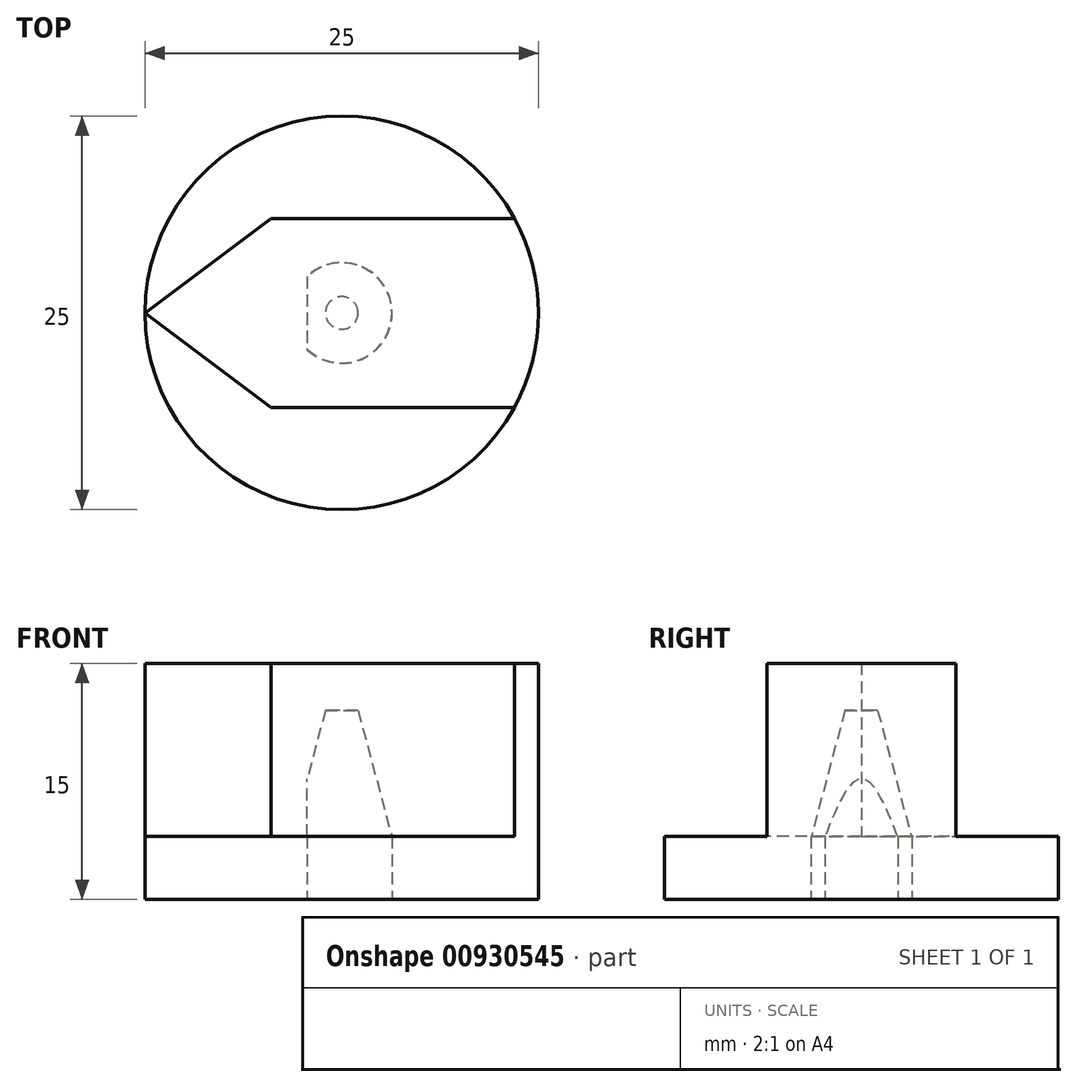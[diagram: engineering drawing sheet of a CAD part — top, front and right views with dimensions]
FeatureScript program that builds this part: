
annotation { "Feature Type Name" : "Feature", "Feature Type Description" : "" }
export const myFeature = defineFeature(function(context is Context, id is Id, definition is map)
    precondition{}
    {
        {
            var Q0;
            Q0=qCreatedBy(makeId("Top.planeOp"),FACE);
            var sketch = newSketch(context, id + "F0", { "sketchPlane" : qUnion([Q0])});
            skCircle(sketch, "E0", {"center": v(0, 0) * mm, "radius": 3.2 * mm, "construction": true});
            skLineSegment(sketch, "E1", {"start": v(-2.2, 2.32) * mm, "end": v(-2.2, -2.32) * mm});
            skLineSegment(sketch, "E2", {"start": v(3.2, 0) * mm, "end": v(-2.2, 0) * mm, "construction": true});
            skArc(sketch, "E3", {"start": v(-2.2, -2.32) * mm, "mid": v(3.2, 0) * mm, "end": v(-2.2, 2.32) * mm});
            skCircle(sketch, "E4", {"center": v(0, 0) * mm, "radius": 12.5 * mm});
            skSolve(sketch);
        }
        {
            var Q0;
            Q0=qSketchRegion(id+"F0",true);
            extrude(context, id + "F1", {"entities" : qUnion([Q0]), "depth" : 4 * mm, "offsetDistance" : 25 * mm});
        }
        {
            var Q0;
            Q0=makeQuery(id+"F1.opExtrude","CAP_FACE",FACE,{"disambiguationData":[OSD([sQuery(id+"F0.wireOp",EDGE,"E1"),sQuery(id+"F0.wireOp",EDGE,"E3"),sQuery(id+"F0.wireOp",EDGE,"E4")])],"isStart":false});
            var sketch = newSketch(context, id + "F2", { "sketchPlane" : qUnion([Q0])});
            skLineSegment(sketch, "E5", {"start": v(-12.5, 0) * mm, "end": v(-4.5, 6) * mm});
            skLineSegment(sketch, "E6", {"start": v(-4.5, 6) * mm, "end": v(10.97, 6) * mm});
            skArc(sketch, "E7", {"start": v(12.5, 0) * mm, "mid": v(12.11, 3.1) * mm, "end": v(10.97, 6) * mm});
            skLineSegment(sketch, "E8", {"start": v(-12.5, 0) * mm, "end": v(12.5, 0) * mm, "construction": true});
            skLineSegment(sketch, "E9.MirrorCS", {"start": v(-12.5, 0) * mm, "end": v(-4.5, -6) * mm});
            skLineSegment(sketch, "E10.MirrorCS", {"start": v(-4.5, -6) * mm, "end": v(10.97, -6) * mm});
            skArc(sketch, "E11.MirrorCS", {"start": v(12.5, 0) * mm, "mid": v(12.11, -3.1) * mm, "end": v(10.97, -6) * mm});
            skCircle(sketch, "E12", {"center": v(0, 0) * mm, "radius": 0.5 * mm});
            skSolve(sketch);
        }
        {
            var Q0;
            Q0=qSketchRegion(id+"F2",true);
            extrude(context, id + "F3", {"entities" : qUnion([Q0]), "operationType" : NewBodyOperationType.ADD, "depth" : 8 * mm, "offsetDistance" : 25 * mm});
        }
        {
            var Q0;
            Q0=makeQuery(id+"F3.opExtrude","CAP_EDGE",EDGE,{"disambiguationData":[OSD([sQuery(id+"F2.wireOp",EDGE,"E12")])],"isStart":true});
            chamfer(context, id + "F4", {"entities" : qUnion([Q0]), "chamferType" : ChamferType.OFFSET_ANGLE, "width" : 10 * mm, "oppositeDirection" : true, "angle" : 15 * degree, "tangentPropagation" : true});
        }
        {
            var Q0;
            Q0=makeQuery(id+"F3.opExtrude","CAP_FACE",FACE,{"disambiguationData":[OSD([sQuery(id+"F2.wireOp",EDGE,"E5"),sQuery(id+"F2.wireOp",EDGE,"E6"),sQuery(id+"F2.wireOp",EDGE,"E7"),sQuery(id+"F2.wireOp",EDGE,"E9.MirrorCS"),sQuery(id+"F2.wireOp",EDGE,"E10.MirrorCS"),sQuery(id+"F2.wireOp",EDGE,"E11.MirrorCS"),sQuery(id+"F2.wireOp",EDGE,"E12")])],"isStart":false});
            var sketch = newSketch(context, id + "F5", { "sketchPlane" : qUnion([Q0])});
            skLineSegment(sketch, "E13", {"start": v(-12.5, 0) * mm, "end": v(-4.5, 6) * mm});
            skLineSegment(sketch, "E14", {"start": v(-4.5, 6) * mm, "end": v(10.97, 6) * mm});
            skLineSegment(sketch, "E15", {"start": v(-12.5, 0) * mm, "end": v(-4.5, -6) * mm});
            skLineSegment(sketch, "E16", {"start": v(-4.5, -6) * mm, "end": v(10.97, -6) * mm});
            skArc(sketch, "E17", {"start": v(10.97, -6) * mm, "mid": v(12.5, 0) * mm, "end": v(10.97, 6) * mm});
            skSolve(sketch);
        }
        {
            var Q0;
            Q0=qSketchRegion(id+"F5",true);
            extrude(context, id + "F6", {"entities" : qUnion([Q0]), "operationType" : NewBodyOperationType.ADD, "depth" : 3 * mm, "offsetDistance" : 25 * mm});
        }
    });
